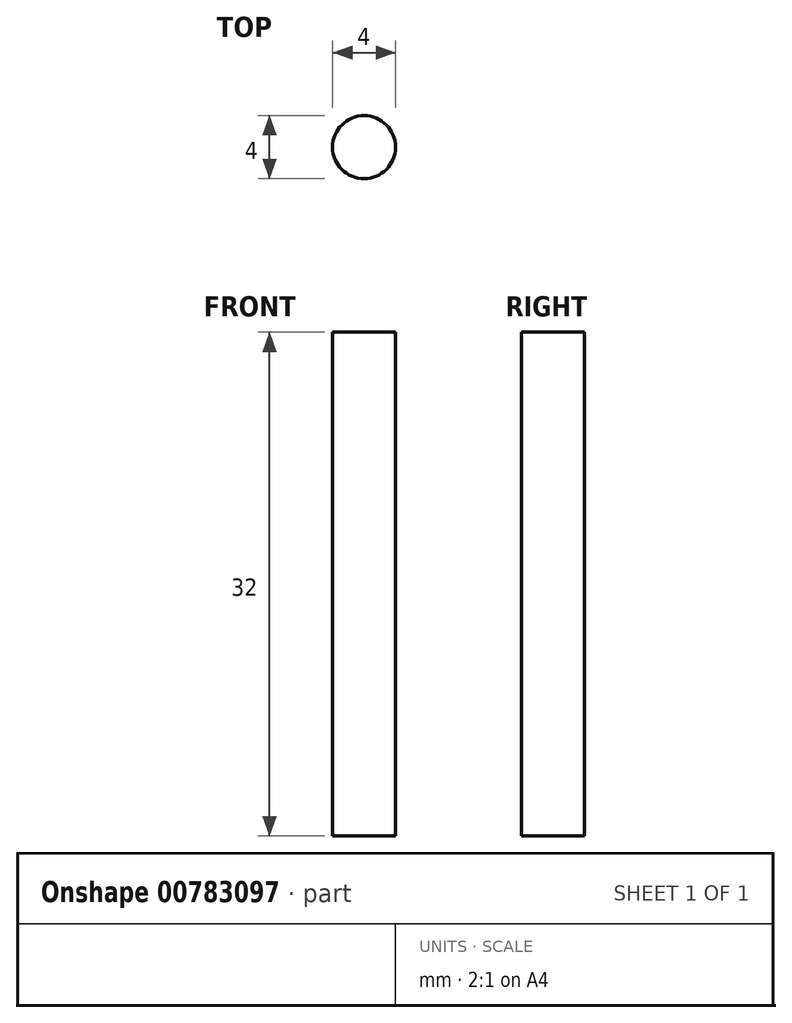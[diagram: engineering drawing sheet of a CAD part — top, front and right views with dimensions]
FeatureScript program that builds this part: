
annotation { "Feature Type Name" : "Feature", "Feature Type Description" : "" }
export const myFeature = defineFeature(function(context is Context, id is Id, definition is map)
    precondition{}
    {
        {
            var Q0;
            Q0=qCreatedBy(makeId("Top.planeOp"),FACE);
            var sketch = newSketch(context, id + "F0", { "sketchPlane" : qUnion([Q0])});
            skCircle(sketch, "E0", {"center": v(-56.45, 15.47) * mm, "radius": 2 * mm});
            skSolve(sketch);
        }
        {
            var Q0;
            Q0=makeQuery(id+"F0.imprint","IMPRINT",FACE,{"disambiguationData":[TD([[makeQuery(id+"F0.imprint","IMPRINT",EDGE,{"derivedFrom":sQuery(id+"F0.wireOp",EDGE,"E0")}),1.0]])]});
            extrude(context, id + "F1", {"entities" : qUnion([Q0]), "depth" : 32 * mm, "offsetDistance" : 25 * mm});
        }
    });
